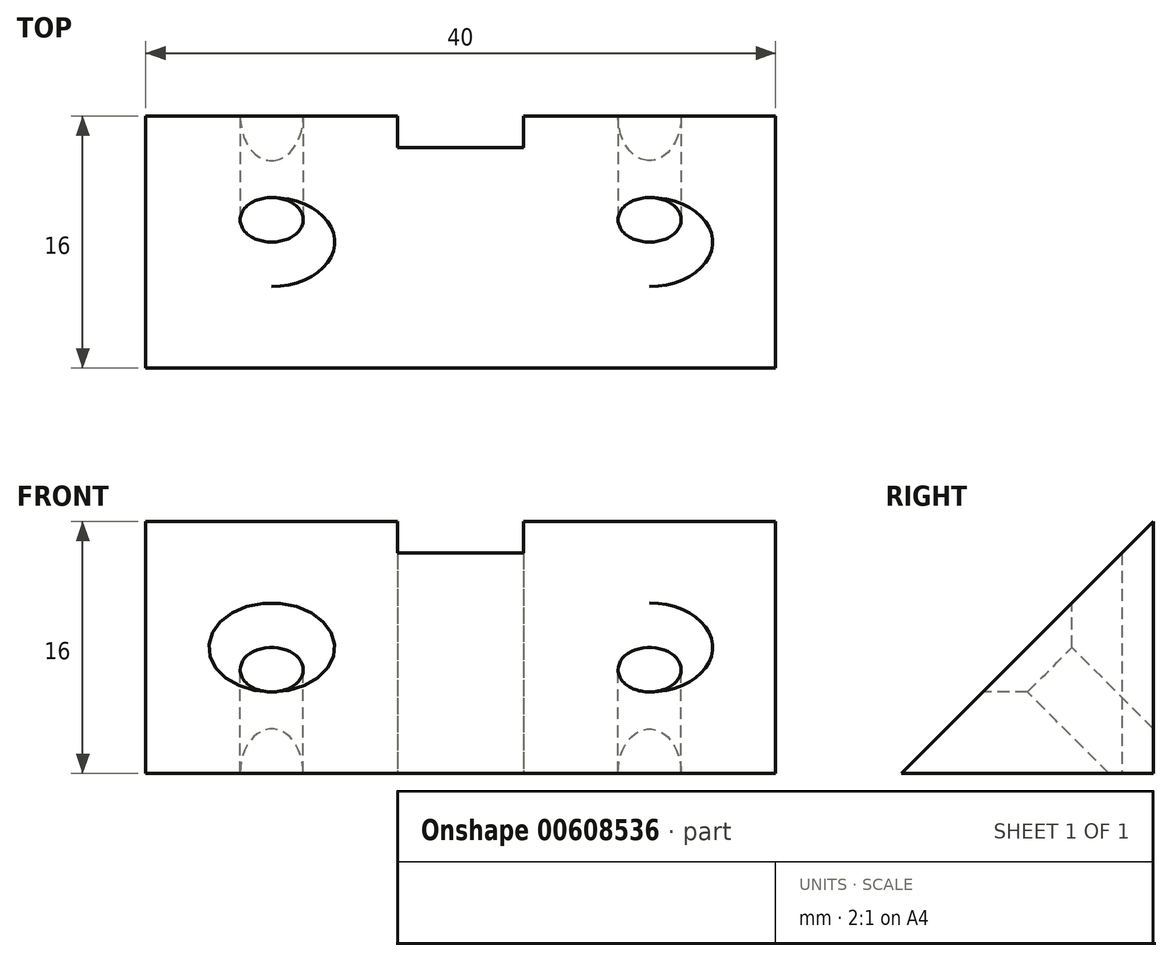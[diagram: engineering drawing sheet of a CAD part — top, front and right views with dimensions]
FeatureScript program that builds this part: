
annotation { "Feature Type Name" : "Feature", "Feature Type Description" : "" }
export const myFeature = defineFeature(function(context is Context, id is Id, definition is map)
    precondition{}
    {
        {
            assignVariable(context, id + "F0", {"name" : "gm", "anyValue" : 8});
        }
        {
            var Q0;
            Q0=qCreatedBy(makeId("Right.planeOp"),FACE);
            var sketch = newSketch(context, id + "F1", { "sketchPlane" : qUnion([Q0])});
            skLineSegment(sketch, "E0", {"start": v(0, 0) * mm, "end": v(0, 16) * mm});
            skLineSegment(sketch, "E1", {"start": v(0, 16) * mm, "end": v(-16, 0) * mm});
            skLineSegment(sketch, "E2", {"start": v(-16, 0) * mm, "end": v(0, 0) * mm});
            skSolve(sketch);
        }
        {
            var Q0;
            Q0=makeQuery(id+"F1.imprint","IMPRINT",FACE,{"disambiguationData":[TD([[makeQuery(id+"F1.imprint","IMPRINT",EDGE,{"derivedFrom":sQuery(id+"F1.wireOp",EDGE,"E0")}),1.0]])]});
            extrude(context, id + "F2", {"entities" : qUnion([Q0]), "endBound" : BoundingType.SYMMETRIC, "depth" : (getVariable(context, 'gm') * 5) * mm, "offsetDistance" : 25 * mm});
        }
        {
            var Q0;
            Q0=makeQuery(id+"F2.opExtrude","SWEPT_FACE",FACE,{"disambiguationData":[OSD([sQuery(id+"F1.wireOp",EDGE,"E1")])]});
            var sketch = newSketch(context, id + "F3", { "sketchPlane" : qUnion([Q0])});
            skPoint(sketch, "E3", {"position": v(-12, 0) * mm});
            skSolve(sketch);
        }
        {
            var Q0;
            Q0=sQuery(id+"F3.wireOp",VERTEX,"E3");
            var Q1;
            Q1=makeQuery(id+"F2.opExtrude","SWEPT_BODY",BODY,{"disambiguationData":[OSD([sQuery(id+"F1.wireOp",EDGE,"E0"),sQuery(id+"F1.wireOp",EDGE,"E1"),sQuery(id+"F1.wireOp",EDGE,"E2")])]});
            hole(context, id + "F4", {"style" : HoleStyle.C_SINK, "endStyle" : HoleEndStyle.THROUGH, "holeDiameter" : 4 * mm, "cSinkDiameter" : 8 * mm, "cSinkAngle" : 90 * degree, "majorDiameter" : 5 * mm, "isTappedThrough" : true, "tappedDepth" : 12 * mm, "tapClearance" : 3, "locations" : qUnion([Q0]), "scope" : qUnion([Q1])});
        }
        {
            var Q0;
            Q0=makeQuery(id+"F2.opExtrude","SWEPT_BODY",BODY,{"disambiguationData":[OSD([sQuery(id+"F1.wireOp",EDGE,"E0"),sQuery(id+"F1.wireOp",EDGE,"E1"),sQuery(id+"F1.wireOp",EDGE,"E2")])]});
            var Q1;
            Q1=qCreatedBy(makeId("Right.planeOp"),FACE);
            mirror(context, id + "F5", {"operationType" : NewBodyOperationType.INTERSECT, "entities" : qUnion([Q0]), "mirrorPlane" : qUnion([Q1])});
        }
        {
            var Q0;
            Q0=makeQuery(id+"F2.opExtrude","SWEPT_FACE",FACE,{"disambiguationData":[OSD([sQuery(id+"F1.wireOp",EDGE,"E2")])]});
            var sketch = newSketch(context, id + "F6", { "sketchPlane" : qUnion([Q0])});
            skLineSegment(sketch, "E4.0", {"start": v(10, 0) * mm, "end": v(-10, 0) * mm});
            skLineSegment(sketch, "E5", {"start": v(0, 0) * mm, "end": v(0, 16) * mm, "construction": true});
            skLineSegment(sketch, "E6", {"start": v(4, 0) * mm, "end": v(4, 2) * mm});
            skLineSegment(sketch, "E7", {"start": v(4, 2) * mm, "end": v(-4, 2) * mm});
            skPoint(sketch, "E7.endSnap0", {"position": v(0, 2) * mm});
            skLineSegment(sketch, "E8", {"start": v(-4, 2) * mm, "end": v(-4, 0) * mm});
            skSolve(sketch);
        }
        {
            var Q0;
            {var subQ0=sQuery(id+"F6.wireOp",EDGE,"E6");Q0=makeQuery(id+"F6.imprint","IMPRINT",FACE,{"disambiguationData":[TD([[makeQuery(id+"F6.imprint","IMPRINT",EDGE,{"derivedFrom":subQ0}),1.0]])]});}
            extrude(context, id + "F7", {"entities" : qUnion([Q0]), "operationType" : NewBodyOperationType.REMOVE, "endBound" : BoundingType.THROUGH_ALL, "oppositeDirection" : true, "depth" : 25 * mm, "offsetDistance" : 25 * mm});
        }
    });
